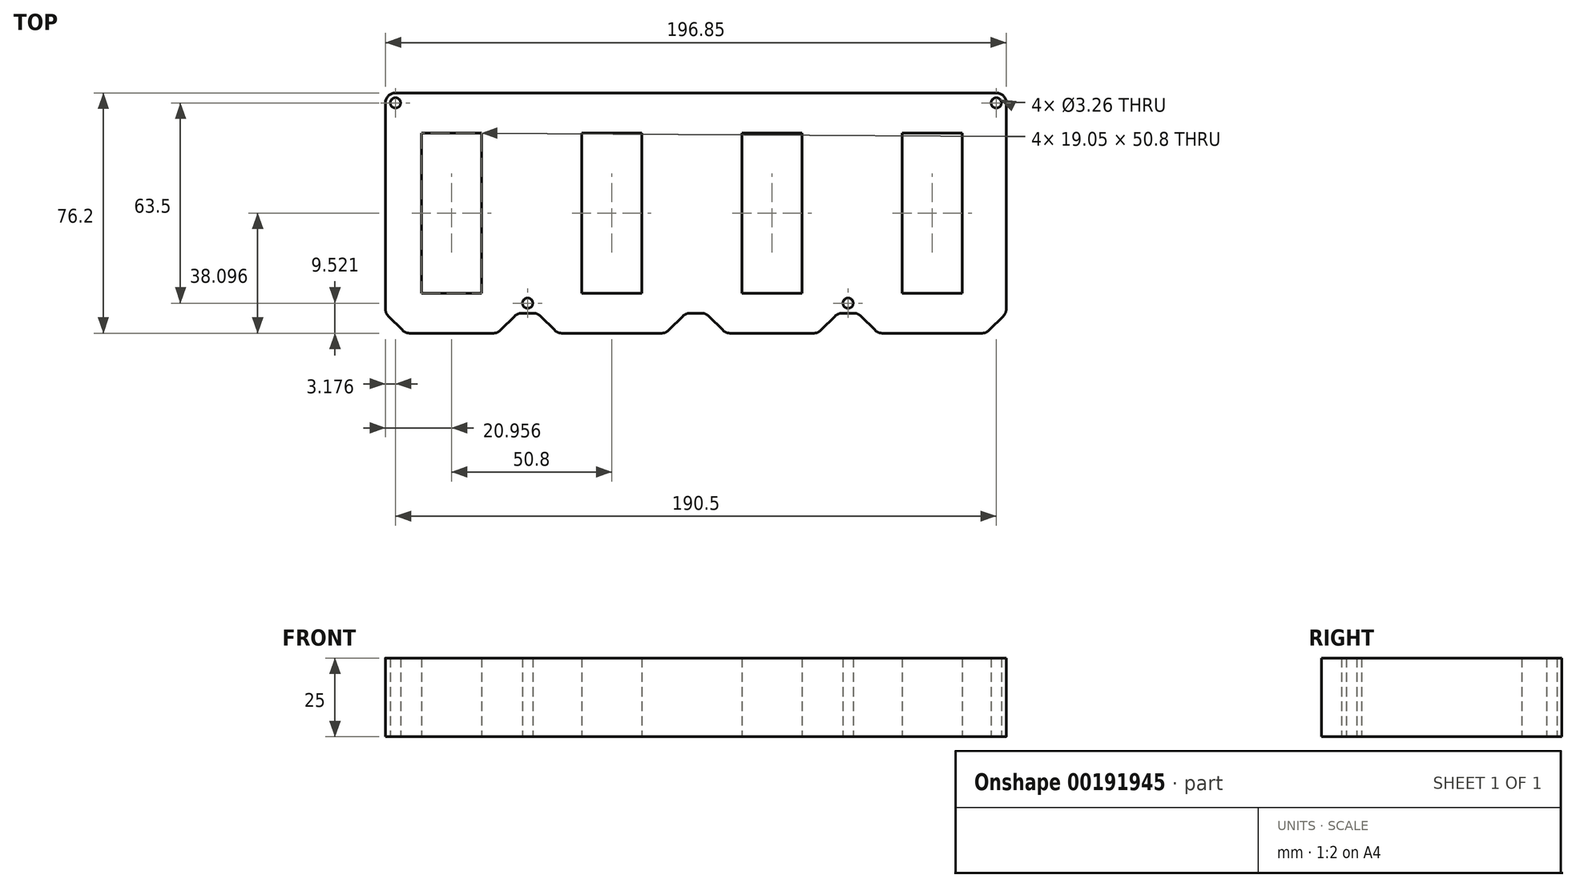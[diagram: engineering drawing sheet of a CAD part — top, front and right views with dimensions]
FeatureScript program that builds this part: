
annotation { "Feature Type Name" : "Feature", "Feature Type Description" : "" }
export const myFeature = defineFeature(function(context is Context, id is Id, definition is map)
    precondition{}
    {
        {
            var Q0;
            Q0=qCreatedBy(makeId("Top.planeOp"),FACE);
            var sketch = newSketch(context, id + "F0", { "sketchPlane" : qUnion([Q0])});
            skLineSegment(sketch, "E0", {"start": v(-1668.07, -557.47) * mm, "end": v(-1636.41, -557.47) * mm});
            skLineSegment(sketch, "E1", {"start": v(-1634.17, -556.54) * mm, "end": v(-1629.68, -552.05) * mm});
            skLineSegment(sketch, "E2", {"start": v(-1627.43, -551.12) * mm, "end": v(-1623.71, -551.12) * mm});
            skLineSegment(sketch, "E3", {"start": v(-1621.47, -552.05) * mm, "end": v(-1616.98, -556.54) * mm});
            skLineSegment(sketch, "E4", {"start": v(-1614.73, -557.47) * mm, "end": v(-1588.15, -557.47) * mm});
            skLineSegment(sketch, "E5", {"start": v(-1585.9, -556.54) * mm, "end": v(-1581.42, -552.05) * mm});
            skLineSegment(sketch, "E6", {"start": v(-1579.17, -551.12) * mm, "end": v(-1575.45, -551.12) * mm});
            skLineSegment(sketch, "E7", {"start": v(-1573.2, -552.05) * mm, "end": v(-1568.72, -556.54) * mm});
            skLineSegment(sketch, "E8", {"start": v(-1566.47, -557.47) * mm, "end": v(-1534.81, -557.47) * mm});
            skLineSegment(sketch, "E9", {"start": v(-1532.57, -556.54) * mm, "end": v(-1528.08, -552.05) * mm});
            skLineSegment(sketch, "E10", {"start": v(-1527.15, -549.8) * mm, "end": v(-1527.15, -484.45) * mm});
            skLineSegment(sketch, "E11", {"start": v(-1670.32, -556.54) * mm, "end": v(-1674.8, -552.05) * mm});
            skLineSegment(sketch, "E12", {"start": v(-1677.05, -551.12) * mm, "end": v(-1680.77, -551.12) * mm});
            skLineSegment(sketch, "E13", {"start": v(-1683.02, -552.05) * mm, "end": v(-1687.5, -556.54) * mm});
            skLineSegment(sketch, "E14", {"start": v(-1689.75, -557.47) * mm, "end": v(-1716.33, -557.47) * mm});
            skLineSegment(sketch, "E15", {"start": v(-1718.58, -556.54) * mm, "end": v(-1723.07, -552.05) * mm});
            skLineSegment(sketch, "E16", {"start": v(-1724, -549.8) * mm, "end": v(-1724, -484.45) * mm});
            skLineSegment(sketch, "E17.bottom", {"start": v(-1693.52, -493.97) * mm, "end": v(-1712.57, -493.97) * mm});
            skLineSegment(sketch, "E17.top", {"start": v(-1693.52, -544.77) * mm, "end": v(-1712.57, -544.77) * mm});
            skLineSegment(sketch, "E17.left", {"start": v(-1693.52, -493.97) * mm, "end": v(-1693.52, -544.77) * mm});
            skLineSegment(sketch, "E17.right", {"start": v(-1712.57, -493.97) * mm, "end": v(-1712.57, -544.77) * mm});
            skPoint(sketch, "E17.middle", {"position": v(-1703.04, -519.37) * mm});
            skPoint(sketch, "E17.middle.positionSnap0", {"position": v(-1703.04, -557.47) * mm});
            skPoint(sketch, "E17.centerSnap0", {"position": v(-1703.04, -557.47) * mm});
            skLineSegment(sketch, "E18.bottom", {"start": v(-1642.72, -493.97) * mm, "end": v(-1661.77, -493.97) * mm});
            skLineSegment(sketch, "E18.top", {"start": v(-1642.72, -544.77) * mm, "end": v(-1661.77, -544.77) * mm});
            skLineSegment(sketch, "E18.left", {"start": v(-1642.72, -493.97) * mm, "end": v(-1642.72, -544.77) * mm});
            skLineSegment(sketch, "E18.right", {"start": v(-1661.77, -493.97) * mm, "end": v(-1661.77, -544.77) * mm});
            skPoint(sketch, "E18.middle", {"position": v(-1652.24, -519.37) * mm});
            skPoint(sketch, "E18.middle.positionSnap0", {"position": v(-1652.24, -557.47) * mm});
            skPoint(sketch, "E18.centerSnap0", {"position": v(-1652.24, -557.47) * mm});
            skLineSegment(sketch, "E19.bottom", {"start": v(-1591.92, -493.97) * mm, "end": v(-1610.97, -493.97) * mm});
            skLineSegment(sketch, "E19.top", {"start": v(-1591.92, -544.77) * mm, "end": v(-1610.97, -544.77) * mm});
            skLineSegment(sketch, "E19.left", {"start": v(-1591.92, -493.97) * mm, "end": v(-1591.92, -544.77) * mm});
            skLineSegment(sketch, "E19.right", {"start": v(-1610.97, -493.97) * mm, "end": v(-1610.97, -544.77) * mm});
            skPoint(sketch, "E19.middle", {"position": v(-1601.44, -519.37) * mm});
            skPoint(sketch, "E19.middle.positionSnap0", {"position": v(-1601.44, -557.47) * mm});
            skPoint(sketch, "E19.centerSnap0", {"position": v(-1601.44, -557.47) * mm});
            skLineSegment(sketch, "E20.bottom", {"start": v(-1541.12, -493.97) * mm, "end": v(-1560.17, -493.97) * mm});
            skLineSegment(sketch, "E20.top", {"start": v(-1541.12, -544.77) * mm, "end": v(-1560.17, -544.77) * mm});
            skLineSegment(sketch, "E20.left", {"start": v(-1541.12, -493.97) * mm, "end": v(-1541.12, -544.77) * mm});
            skLineSegment(sketch, "E20.right", {"start": v(-1560.17, -493.97) * mm, "end": v(-1560.17, -544.77) * mm});
            skPoint(sketch, "E20.middle", {"position": v(-1550.64, -519.37) * mm});
            skPoint(sketch, "E20.middle.positionSnap0", {"position": v(-1550.64, -557.47) * mm});
            skPoint(sketch, "E20.centerSnap0", {"position": v(-1550.64, -557.47) * mm});
            skLineSegment(sketch, "E21", {"start": v(-1720.82, -481.27) * mm, "end": v(-1530.32, -481.27) * mm});
            skPoint(sketch, "E22.visualSharp", {"position": v(-1724, -481.27) * mm});
            skArc(sketch, "E22.filletArc", {"start": v(-1720.82, -481.27) * mm, "mid": v(-1723.07, -482.2) * mm, "end": v(-1724, -484.45) * mm});
            skPoint(sketch, "E23.visualSharp", {"position": v(-1527.15, -481.27) * mm});
            skArc(sketch, "E23.filletArc", {"start": v(-1527.15, -484.45) * mm, "mid": v(-1528.08, -482.2) * mm, "end": v(-1530.32, -481.27) * mm});
            skPoint(sketch, "E24.visualSharp", {"position": v(-1527.15, -551.12) * mm});
            skArc(sketch, "E24.filletArc", {"start": v(-1528.08, -552.05) * mm, "mid": v(-1527.4, -551.02) * mm, "end": v(-1527.15, -549.8) * mm});
            skPoint(sketch, "E25.visualSharp", {"position": v(-1533.5, -557.47) * mm});
            skArc(sketch, "E25.filletArc", {"start": v(-1534.81, -557.47) * mm, "mid": v(-1533.6, -557.23) * mm, "end": v(-1532.57, -556.54) * mm});
            skPoint(sketch, "E26.visualSharp", {"position": v(-1567.79, -557.47) * mm});
            skArc(sketch, "E26.filletArc", {"start": v(-1568.72, -556.54) * mm, "mid": v(-1567.69, -557.23) * mm, "end": v(-1566.47, -557.47) * mm});
            skPoint(sketch, "E27.visualSharp", {"position": v(-1574.14, -551.12) * mm});
            skArc(sketch, "E27.filletArc", {"start": v(-1573.2, -552.05) * mm, "mid": v(-1574.24, -551.37) * mm, "end": v(-1575.45, -551.12) * mm});
            skPoint(sketch, "E28.visualSharp", {"position": v(-1580.49, -551.12) * mm});
            skArc(sketch, "E28.filletArc", {"start": v(-1579.17, -551.12) * mm, "mid": v(-1580.39, -551.37) * mm, "end": v(-1581.42, -552.05) * mm});
            skPoint(sketch, "E29.visualSharp", {"position": v(-1586.84, -557.47) * mm});
            skArc(sketch, "E29.filletArc", {"start": v(-1588.15, -557.47) * mm, "mid": v(-1586.94, -557.23) * mm, "end": v(-1585.9, -556.54) * mm});
            skPoint(sketch, "E30.visualSharp", {"position": v(-1616.05, -557.47) * mm});
            skArc(sketch, "E30.filletArc", {"start": v(-1616.98, -556.54) * mm, "mid": v(-1615.95, -557.23) * mm, "end": v(-1614.73, -557.47) * mm});
            skPoint(sketch, "E31.visualSharp", {"position": v(-1628.75, -551.12) * mm});
            skArc(sketch, "E31.filletArc", {"start": v(-1627.43, -551.12) * mm, "mid": v(-1628.65, -551.37) * mm, "end": v(-1629.68, -552.05) * mm});
            skPoint(sketch, "E32.visualSharp", {"position": v(-1635.1, -557.47) * mm});
            skArc(sketch, "E32.filletArc", {"start": v(-1636.41, -557.47) * mm, "mid": v(-1635.2, -557.23) * mm, "end": v(-1634.17, -556.54) * mm});
            skPoint(sketch, "E33.visualSharp", {"position": v(-1622.4, -551.12) * mm});
            skArc(sketch, "E33.filletArc", {"start": v(-1621.47, -552.05) * mm, "mid": v(-1622.5, -551.37) * mm, "end": v(-1623.71, -551.12) * mm});
            skPoint(sketch, "E34.visualSharp", {"position": v(-1669.39, -557.47) * mm});
            skArc(sketch, "E34.filletArc", {"start": v(-1670.32, -556.54) * mm, "mid": v(-1669.29, -557.23) * mm, "end": v(-1668.07, -557.47) * mm});
            skPoint(sketch, "E35.visualSharp", {"position": v(-1675.74, -551.12) * mm});
            skArc(sketch, "E35.filletArc", {"start": v(-1674.8, -552.05) * mm, "mid": v(-1675.84, -551.37) * mm, "end": v(-1677.05, -551.12) * mm});
            skPoint(sketch, "E36.visualSharp", {"position": v(-1682.09, -551.12) * mm});
            skArc(sketch, "E36.filletArc", {"start": v(-1680.77, -551.12) * mm, "mid": v(-1681.99, -551.37) * mm, "end": v(-1683.02, -552.05) * mm});
            skPoint(sketch, "E37.visualSharp", {"position": v(-1688.44, -557.47) * mm});
            skArc(sketch, "E37.filletArc", {"start": v(-1689.75, -557.47) * mm, "mid": v(-1688.54, -557.23) * mm, "end": v(-1687.5, -556.54) * mm});
            skPoint(sketch, "E38.visualSharp", {"position": v(-1717.65, -557.47) * mm});
            skArc(sketch, "E38.filletArc", {"start": v(-1718.58, -556.54) * mm, "mid": v(-1717.55, -557.23) * mm, "end": v(-1716.33, -557.47) * mm});
            skPoint(sketch, "E39.visualSharp", {"position": v(-1724, -551.12) * mm});
            skArc(sketch, "E39.filletArc", {"start": v(-1724, -549.8) * mm, "mid": v(-1723.76, -551.02) * mm, "end": v(-1723.07, -552.05) * mm});
            skCircle(sketch, "E40", {"center": v(-1720.82, -484.45) * mm, "radius": 1.63 * mm});
            skCircle(sketch, "E41", {"center": v(-1530.32, -484.45) * mm, "radius": 1.63 * mm});
            skCircle(sketch, "E42", {"center": v(-1577.31, -547.95) * mm, "radius": 1.63 * mm});
            skPoint(sketch, "E42.centerSnap0", {"position": v(-1577.31, -551.12) * mm});
            skCircle(sketch, "E43", {"center": v(-1678.91, -547.95) * mm, "radius": 1.63 * mm});
            skPoint(sketch, "E43.centerSnap0", {"position": v(-1678.91, -551.12) * mm});
            skSolve(sketch);
        }
        {
            var Q0;
            Q0 = qSketchRegion(id + "F0", true);
            extrude(context, id + "F1", {"entities" : qUnion([Q0]), "depth" : 25 * mm});
        }
    });
